# Revit family: 4L-P-ID
name_source: partatom
category: Lighting Fixtures
revit_build: Autodesk Revit 2013 (Build: 20120221_2030(x64)
units: mm (PartAtom-declared; Revit-internal decimal feet)

## types (6) — shared parameters
Apparent Load = 56 VA
Connector Description = Lighting Connector
Default Elevation = 48"
Description = MOD 4 LED Pendant Indirect/Direct
Direct Output/ft = D110-1100
Downlight diffuser = Downlight diffuser
Fixture Length = MOD 4 : 4'
Indirect Output/ft = I120-1200
Lamp = LED
Load Classification = Lighting
Manufacturer = LITECONTROL
Manufacturer Fax = 781-293-2849
Model = 4L-P-ID
Pendent Height = 9"
Power Factor = 1
Product Documentation Link = http://cdn.litecontrol.com
Product Page URL = http://www.litecontrol.com
Reflector Finish = Hubbell-White Glass
URL = http://www.litecontrol.com
Uplight distribution = Low Peak Angle
Voltage = 120 V
Wattage Comments = Variable Intensity technology provides specifiable lumen output/wattage
Watts = 56 W

## per-type parameters (varying)
| type | Product Material |
| 4L-P-ID-C1 | Paint - Hubbell - Matte White |
| 4L-P-ID-C2 | Paint - Hubbell - Textured Matte White |
| 4L-P-ID-C3 | Paint - Hubbell - Light Silver |
| 4L-P-ID-C4 | Paint - Hubbell - Machined Aluminum |
| 4L-P-ID-C5 | Paint - Hubbell - Carbon Black |
| 4L-P-ID-C6 | Paint - Hubbell - Textured Camera Black |

## geometry (parser evidence)
native form markers: Blend x10, Sweep x4
no freeform markers — native parametric forms only
